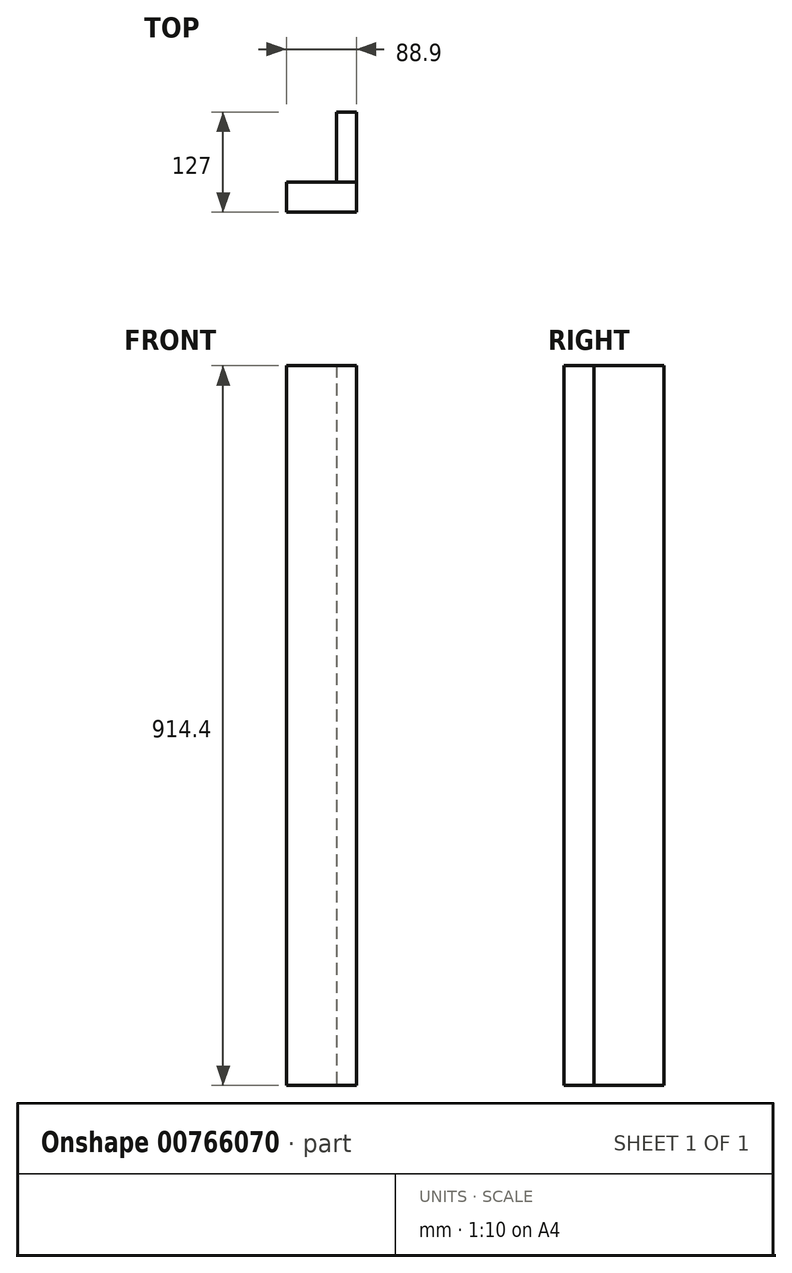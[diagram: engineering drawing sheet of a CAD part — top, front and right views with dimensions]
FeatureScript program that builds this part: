
annotation { "Feature Type Name" : "Feature", "Feature Type Description" : "" }
export const myFeature = defineFeature(function(context is Context, id is Id, definition is map)
    precondition{}
    {
        {
            var Q0;
            Q0=qCreatedBy(makeId("Front.planeOp"),FACE);
            var sketch = newSketch(context, id + "F0", { "sketchPlane" : qUnion([Q0])});
            skLineSegment(sketch, "E0.bottom", {"start": v(-88.9, 550.36) * mm, "end": v(0, 550.36) * mm});
            skLineSegment(sketch, "E0.top", {"start": v(-88.9, -364.04) * mm, "end": v(0, -364.04) * mm});
            skLineSegment(sketch, "E0.left", {"start": v(-88.9, 550.36) * mm, "end": v(-88.9, -364.04) * mm});
            skLineSegment(sketch, "E0.right", {"start": v(0, 550.36) * mm, "end": v(0, -364.04) * mm});
            skSolve(sketch);
        }
        {
            var Q0;
            Q0=qSketchRegion(id+"F0",true);
            extrude(context, id + "F1", {"entities" : qUnion([Q0]), "depth" : 38.1 * mm, "offsetDistance" : 25.4 * mm});
        }
        {
            var Q0;
            Q0=qCreatedBy(makeId("Right.planeOp"),FACE);
            var sketch = newSketch(context, id + "F2", { "sketchPlane" : qUnion([Q0])});
            skLineSegment(sketch, "E1.bottom", {"start": v(88.9, 550.36) * mm, "end": v(0, 550.36) * mm});
            skLineSegment(sketch, "E1.top", {"start": v(88.9, -364.04) * mm, "end": v(0, -364.04) * mm});
            skLineSegment(sketch, "E1.left", {"start": v(88.9, 550.36) * mm, "end": v(88.9, -364.04) * mm});
            skLineSegment(sketch, "E1.right", {"start": v(0, 550.36) * mm, "end": v(0, -364.04) * mm});
            skSolve(sketch);
        }
        {
            var Q0;
            Q0=qSketchRegion(id+"F2",true);
            extrude(context, id + "F3", {"entities" : qUnion([Q0]), "oppositeDirection" : true, "depth" : 25.4 * mm, "offsetDistance" : 25.4 * mm});
        }
    });
